# Revit family: SNS Merlin Natural Gas Detector TFT
name_source: partatom
category: Electrical Equipment
units: mm (PartAtom-declared; Revit-internal decimal feet)

## family parameters
Always vertical = Yes
Cut with Voids When Loaded = No
OmniClass Number = 23.80.30.11.17
OmniClass Title = Distribution Boards and Control Panels
Part Type = Other Panel
Room Calculation Point = No
Round Connector Dimension = Use Diameter
Shared = No
Work Plane-Based = No

## types (1)
- SNS Merlin NG TFT Gas Detector
    Default Height = 4' - 0"
    Description = The TFT range of S&S detectors work in combination with the S&S Merlin range of Gas Detection panels and Utility Controllers. Semi conductor type sensor for industrial and commercial indoor applications. Compact, modern, digital design makes the units aesthetically pleasing and easy to install.

The Natural Gas sensor should be mounted in accordance with certain considerations. Do not position next to burners, heaters or ovens where temperatures above the room ambient may be experienced. It is, if possible, better to mount the sensors on the opposite wall. This is, of course, dependent on the size of the protected area. Natural gas is lighter than air and will therefore rise, meaning the sensor should be mounted 10 Inches from the Ceiling of the protected area. The Natural gas detectors at detection will go into alarm at 10% of the low explosion level. This will trigger isolation of the power supply to the solenoid and as such isolation of the gas supply. This can then be rectified by resolving the leak, allowing the sensor head to clear and resetting the attached Merlin panel.
    Load = 120 VA
    Manufacturer = S&S Northern Ltd.
    Model = SNS Merlin NG TFT Gas Detector
    Product Information = https://snsnorthern.com
    Type Comments = The TFT range of S&S detectors work in combination with the S&S Merlin range of Gas Detection panels and Utility Controllers. Semi conductor type sensor for industrial and commercial indoor applications. Compact, modern, digital design makes the units aesthetically pleasing and easy to install.

The Natural Gas sensor should be mounted in accordance with certain considerations. Do not position next to burners, heaters or ovens where temperatures above the room ambient may be experienced. It is, if possible, better to mount the sensors on the opposite wall. This is, of course, dependent on the size of the protected area. Natural gas is lighter than air and will therefore rise, meaning the sensor should be mounted 10 Inches from the Ceiling of the protected area. The Natural gas detectors at detection will go into alarm at 10% of the low explosion level. This will trigger isolation of the power supply to the solenoid and as such isolation of the gas supply. This can then be rectified by resolving the leak, allowing the sensor head to clear and resetting the attached Merlin panel.
    URL = https://snsnorthern.com
    Voltage = 120VAC

## geometry (parser evidence)
native form markers: Sweep x8
no freeform markers — native parametric forms only
